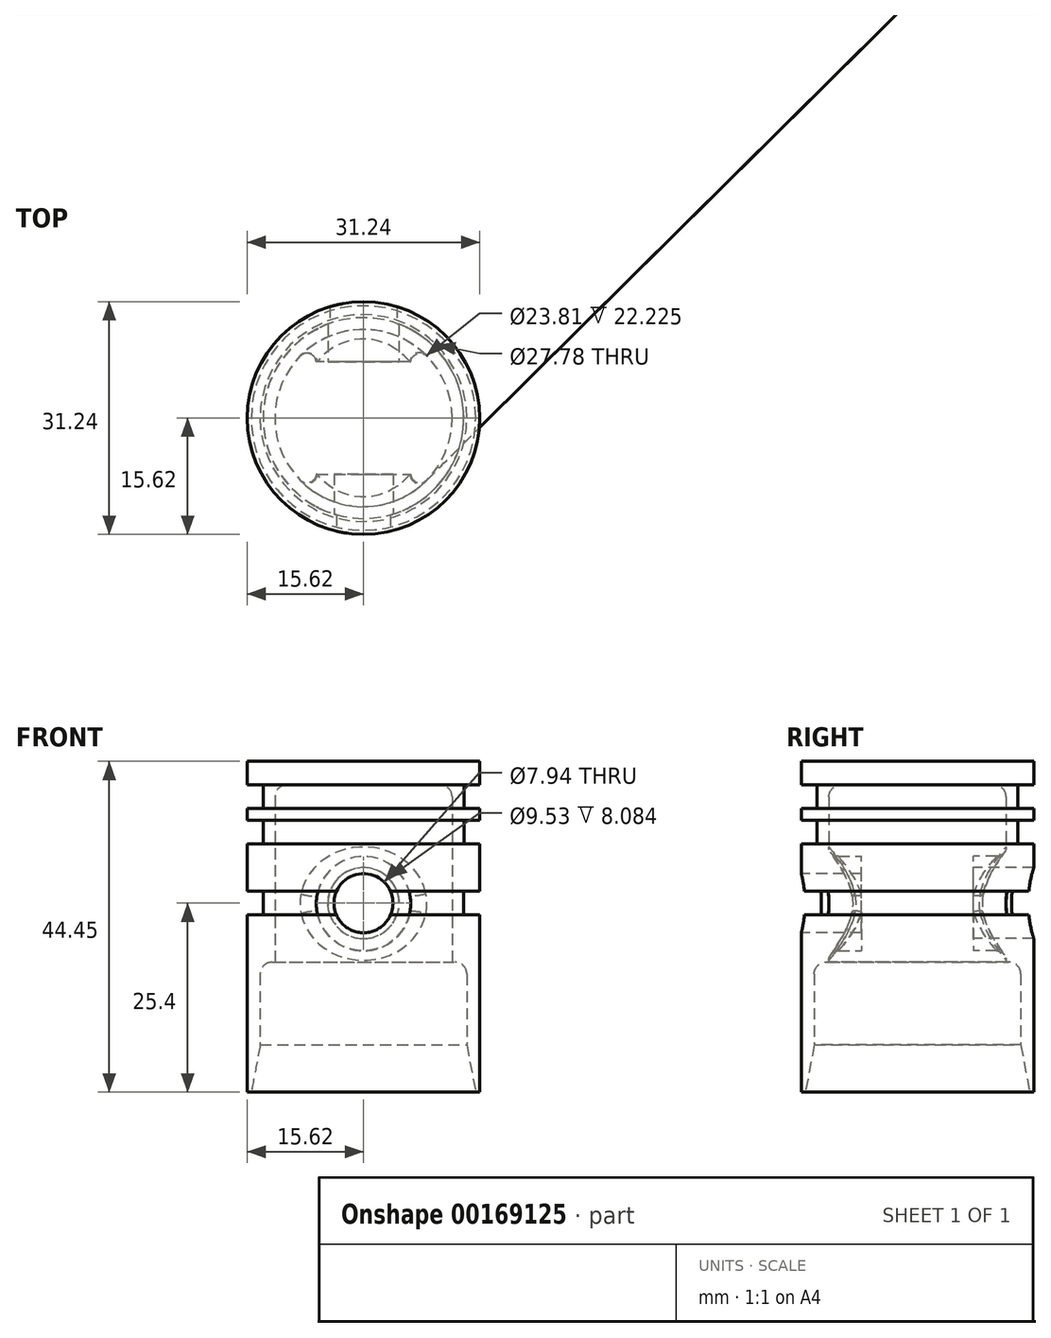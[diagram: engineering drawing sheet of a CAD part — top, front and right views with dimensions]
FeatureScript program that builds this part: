
annotation { "Feature Type Name" : "Feature", "Feature Type Description" : "" }
export const myFeature = defineFeature(function(context is Context, id is Id, definition is map)
    precondition{}
    {
        {
            var Q0;
            Q0=qCreatedBy(makeId("Front.planeOp"),FACE);
            var sketch = newSketch(context, id + "F0", { "sketchPlane" : qUnion([Q0])});
            skLineSegment(sketch, "E0", {"start": v(0, 0) * mm, "end": v(-15.88, 0) * mm});
            skLineSegment(sketch, "E1", {"start": v(-15.88, 0) * mm, "end": v(-15.88, -3.18) * mm});
            skLineSegment(sketch, "E2", {"start": v(-15.88, -3.18) * mm, "end": v(-13.5, -3.18) * mm});
            skLineSegment(sketch, "E3", {"start": v(-13.5, -3.18) * mm, "end": v(-13.5, -6.35) * mm});
            skLineSegment(sketch, "E4", {"start": v(-15.88, -7.94) * mm, "end": v(-13.5, -7.94) * mm});
            skLineSegment(sketch, "E5", {"start": v(-13.5, -7.94) * mm, "end": v(-13.5, -11.11) * mm});
            skLineSegment(sketch, "E6", {"start": v(-13.5, -11.11) * mm, "end": v(-15.87, -11.11) * mm});
            skLineSegment(sketch, "E7", {"start": v(-15.88, -11.11) * mm, "end": v(-15.88, -12.7) * mm});
            skLineSegment(sketch, "E8", {"start": v(-15.87, -44.45) * mm, "end": v(-15.08, -44.45) * mm});
            skLineSegment(sketch, "E9", {"start": v(-11.9, -26.99) * mm, "end": v(-11.9, -4.76) * mm});
            skLineSegment(sketch, "E10", {"start": v(-10.32, -3.18) * mm, "end": v(0, -3.18) * mm});
            skLineSegment(sketch, "E11", {"start": v(-11.9, -26.99) * mm, "end": v(-12.3, -26.99) * mm});
            skLineSegment(sketch, "E12", {"start": v(-13.9, -28.57) * mm, "end": v(-13.9, -38.1) * mm});
            skLineSegment(sketch, "E13", {"start": v(-13.9, -38.1) * mm, "end": v(-15.08, -44.45) * mm});
            skPoint(sketch, "E14.visualSharp", {"position": v(-11.9, -3.18) * mm});
            skArc(sketch, "E14.filletArc", {"start": v(-10.32, -3.18) * mm, "mid": v(-11.44, -3.64) * mm, "end": v(-11.9, -4.76) * mm});
            skPoint(sketch, "E15.visualSharp", {"position": v(-13.9, -26.99) * mm});
            skArc(sketch, "E15.filletArc", {"start": v(-12.3, -26.99) * mm, "mid": v(-13.43, -27.45) * mm, "end": v(-13.9, -28.57) * mm});
            skPoint(sketch, "E16.orphan", {"position": v(-15.88, -6.35) * mm});
            skLineSegment(sketch, "E17", {"start": v(-15.88, -6.35) * mm, "end": v(-13.5, -6.35) * mm});
            skLineSegment(sketch, "E18", {"start": v(-15.62, -17.46) * mm, "end": v(-13.48, -17.46) * mm});
            skLineSegment(sketch, "E19", {"start": v(-13.48, -17.46) * mm, "end": v(-13.48, -20.64) * mm});
            skLineSegment(sketch, "E20", {"start": v(-13.48, -20.64) * mm, "end": v(-15.62, -20.64) * mm});
            skLineSegment(sketch, "E21.trimOffspring", {"start": v(-15.88, -31.75) * mm, "end": v(-15.88, -44.45) * mm});
            skLineSegment(sketch, "E22", {"start": v(-15.87, -12.7) * mm, "end": v(-15.62, -12.7) * mm});
            skLineSegment(sketch, "E23", {"start": v(-15.62, -12.7) * mm, "end": v(-15.62, -17.46) * mm});
            skLineSegment(sketch, "E24", {"start": v(-15.62, -31.75) * mm, "end": v(-15.88, -31.75) * mm});
            skPoint(sketch, "E25.orphan", {"position": v(-15.87, -17.46) * mm});
            skPoint(sketch, "E26.orphan", {"position": v(-15.88, -20.64) * mm});
            skLineSegment(sketch, "E27.trimOffspring", {"start": v(-15.62, -20.64) * mm, "end": v(-15.62, -31.75) * mm});
            skLineSegment(sketch, "E28.trimOffspring", {"start": v(-15.88, -6.35) * mm, "end": v(-15.88, -7.94) * mm});
            skLineSegment(sketch, "E29", {"start": v(0, -3.18) * mm, "end": v(0, 16.33) * mm});
            skSolve(sketch);
        }
        {
            var Q0;
            {var subQ1=sQuery(id+"F0.wireOp",EDGE,"E0");Q0=makeQuery(id+"F0.imprint","IMPRINT",FACE,{"disambiguationData":[TD([[makeQuery(id+"F0.imprint","IMPRINT",EDGE,{"derivedFrom":subQ1}),1.0]])]});}
            var Q1;
            Q1=sQuery(id+"F0.wireOp",EDGE,"E29");
            revolve(context, id + "F1", {"entities" : qUnion([Q0]), "axis" : qUnion([Q1]), "revolveType" : RevolveType.FULL});
        }
        {
            var Q0;
            Q0=qCreatedBy(makeId("Front.planeOp"),FACE);
            var sketch = newSketch(context, id + "F2", { "sketchPlane" : qUnion([Q0])});
            skCircle(sketch, "E30", {"center": v(0, -19.05) * mm, "radius": 4.76 * mm});
            skCircle(sketch, "E31", {"center": v(0, -19.05) * mm, "radius": 3.97 * mm});
            skCircle(sketch, "E32", {"center": v(0, -19.05) * mm, "radius": 6.35 * mm});
            skSolve(sketch);
        }
        {
            var Q0;
            Q0=makeQuery(id+"F2.imprint","IMPRINT",FACE,{"disambiguationData":[TD([[makeQuery(id+"F2.imprint","IMPRINT",EDGE,{"derivedFrom":sQuery(id+"F2.wireOp",EDGE,"E31")}),1.0]])]});
            extrude(context, id + "F3", {"entities" : qUnion([Q0]), "operationType" : NewBodyOperationType.REMOVE, "oppositeDirection" : true, "depth" : 25.4 * mm});
        }
        {
            var Q0;
            Q0=makeQuery(id+"F2.imprint","IMPRINT",FACE,{"disambiguationData":[TD([[makeQuery(id+"F2.imprint","IMPRINT",EDGE,{"derivedFrom":sQuery(id+"F2.wireOp",EDGE,"E31")}),1.0]])]});
            var Q1;
            Q1=makeQuery(id+"F2.imprint","IMPRINT",FACE,{"disambiguationData":[TD([[makeQuery(id+"F2.imprint","IMPRINT",EDGE,{"derivedFrom":sQuery(id+"F2.wireOp",EDGE,"E30")}),1.0]])]});
            extrude(context, id + "F4", {"entities" : qUnion([Q0, Q1]), "operationType" : NewBodyOperationType.REMOVE, "depth" : 25.4 * mm});
        }
        {
            var Q0;
            Q0=qCreatedBy(makeId("Front.planeOp"),FACE);
            var sketch = newSketch(context, id + "F5", { "sketchPlane" : qUnion([Q0])});
            skCircle(sketch, "E33", {"center": v(0, -19.11) * mm, "radius": 6.34 * mm});
            skSolve(sketch);
        }
        {
            var Q0;
            Q0 = qSketchRegion(id + "F5", true);
            extrude(context, id + "F6", {"entities" : qUnion([Q0]), "operationType" : NewBodyOperationType.ADD, "depth" : 25.4 * mm, "hasSecondDirection" : true, "secondDirectionOppositeDirection" : false, "secondDirectionDepth" : 7.54 * mm});
        }
        {
            var Q0;
            Q0 = qSketchRegion(id + "F5", true);
            extrude(context, id + "F7", {"entities" : qUnion([Q0]), "operationType" : NewBodyOperationType.ADD, "oppositeDirection" : true, "depth" : 25.4 * mm, "hasSecondDirection" : true, "secondDirectionOppositeDirection" : true, "secondDirectionDepth" : 7.54 * mm});
        }
        {
            var Q0;
            Q0=makeQuery(id+"F7.boolean.opBoolean","INTERSECT",EDGE,{"derivedFrom":[makeQuery(id+"F1.opRevolve","SWEPT_FACE",FACE,{"disambiguationData":[OSD([sQuery(id+"F0.wireOp",EDGE,"E9")])]}),makeQuery(id+"F7.opExtrude","SWEPT_FACE",FACE,{"disambiguationData":[OSD([sQuery(id+"F5.wireOp",EDGE,"E33")])]})]});
            fillet(context, id + "F8", {"entities" : qUnion([Q0]), "radius" : 1.27 * mm, "tangentPropagation" : true, "allowEdgeOverflow" : false});
        }
        {
            var Q0;
            Q0=makeQuery(id+"F6.boolean.opBoolean","INTERSECT",EDGE,{"derivedFrom":[makeQuery(id+"F1.opRevolve","SWEPT_FACE",FACE,{"disambiguationData":[OSD([sQuery(id+"F0.wireOp",EDGE,"E9")])]}),makeQuery(id+"F6.opExtrude","SWEPT_FACE",FACE,{"disambiguationData":[OSD([sQuery(id+"F5.wireOp",EDGE,"E33")])]})]});
            fillet(context, id + "F9", {"entities" : qUnion([Q0]), "radius" : 1.27 * mm, "tangentPropagation" : true, "allowEdgeOverflow" : false});
        }
        {
            var Q0;
            Q0=makeQuery(id+"F2.imprint","IMPRINT",FACE,{"disambiguationData":[TD([[makeQuery(id+"F2.imprint","IMPRINT",EDGE,{"derivedFrom":sQuery(id+"F2.wireOp",EDGE,"E31")}),1.0]])]});
            extrude(context, id + "F10", {"entities" : qUnion([Q0]), "operationType" : NewBodyOperationType.REMOVE, "oppositeDirection" : true, "depth" : 50.8 * mm, "hasSecondDirection" : true, "secondDirectionOppositeDirection" : false, "secondDirectionDepth" : 25.4 * mm});
        }
        {
            var Q0;
            Q0=makeQuery(id+"F2.imprint","IMPRINT",FACE,{"disambiguationData":[TD([[makeQuery(id+"F2.imprint","IMPRINT",EDGE,{"derivedFrom":sQuery(id+"F2.wireOp",EDGE,"E30")}),1.0]])]});
            extrude(context, id + "F11", {"entities" : qUnion([Q0]), "operationType" : NewBodyOperationType.REMOVE, "oppositeDirection" : true, "depth" : 50.8 * mm});
        }
        {
            var Q0;
            Q0=qCreatedBy(makeId("Top.planeOp"),FACE);
            var sketch = newSketch(context, id + "F12", { "sketchPlane" : qUnion([Q0])});
            skCircle(sketch, "E34", {"center": v(0, 0) * mm, "radius": 15.62 * mm});
            skCircle(sketch, "E35", {"center": v(0, 0) * mm, "radius": 30.73 * mm});
            skCircle(sketch, "E36", {"center": v(0, 0) * mm, "radius": 13.5 * mm});
            skSolve(sketch);
        }
        {
            var Q0;
            Q0=makeQuery(id+"F12.imprint","IMPRINT",FACE,{"disambiguationData":[TD([[makeQuery(id+"F12.imprint","IMPRINT",EDGE,{"derivedFrom":sQuery(id+"F12.wireOp",EDGE,"E34")}),-1.0]])]});
            extrude(context, id + "F13", {"entities" : qUnion([Q0]), "operationType" : NewBodyOperationType.REMOVE, "oppositeDirection" : true, "depth" : 50.8 * mm});
        }
        {
            var Q0;
            Q0=makeQuery(id+"F1.opRevolve","SWEPT_FACE",FACE,{"disambiguationData":[OSD([sQuery(id+"F0.wireOp",EDGE,"E2")])]});
            extrude(context, id + "F14", {"entities" : qUnion([Q0]), "operationType" : NewBodyOperationType.REMOVE, "depth" : 17.46 * mm, "hasSecondDirection" : true, "secondDirectionOppositeDirection" : false, "secondDirectionDepth" : 14.29 * mm});
        }
    });
